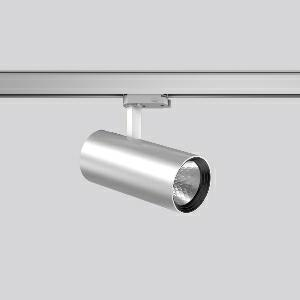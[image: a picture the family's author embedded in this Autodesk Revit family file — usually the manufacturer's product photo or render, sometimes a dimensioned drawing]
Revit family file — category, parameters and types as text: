
# Revit family: deecos_s_mini_742196_004_3_76_3f5c
name_source: partatom
category: Lighting Fixtures
units: mm (PartAtom-declared; Revit-internal decimal feet)

## family parameters
Cut with Voids When Loaded = No
Host = Face
Light Source = No
Part Type = Normal
Room Calculation Point = No
Round Connector Dimension = Use Diameter
Shared = No

## types (1)
- DEECOS S mini (1 x LED Modul 935, 2500 lm, 3500)
    Apparent Load = 20 VA
    Approval mark = CE
    CIE Flux Codes = 99 100 100 100 100
    Color Rendering = 92
    Color Temperature = 3500
    Default Elevation = 1800 mm
    Description = Series: DEECOS S mini
LED surface-mounted projector in modern design with no visible cooling ribs. Housing: die-cast aluminium, powder-coated. Rotation range: 356°. Swivel range: 90°. Black plastic ring and recessed LED to prevent glare from the side. Optical assembly with reflector made of MIRO-Silver with 98% total light reflection for outstanding efficiency - can be changed without tools. Best colour rendering index Ra>90. With adapter for RZB 3-circuit DALI tracks. Suitable for Track on ceiling, Wall track. High quality converter without flickering and stroboscopic effect. The following accessories can be mounted without use of tools: interchangeable lenses, decorative glasses, honeycomb louvre, clear and frosted diffusers, white interchangeable plastic ring. 
Colour: silver
Diameter: 87 mm
Height: 214 mm
Lamp: LED
Socket: without socket
Colour temperature: 3500K
Colour rendering index (CRI): 92
System power: 20 W
Rated luminous flux: 2500 lm
Luminous efficiency: 125 lm/W
Control gear: Converter, dimmable, DALI
Protection class: I
Type of protection: IP 20
    Height = 214 mm
    Lamp = 1 x LED Modul 935
    Lamp Light Flux = 2500 lm
    Lamp count = 1
    Length = 87 mm
    Lifetime = 50000 h
    Luminous efficacy = 125 lm/W
    Manufacturer = RZB
    ModVariant = No
    Model = 742196.004.3.76
    Mounting Place = Ceiling
    Mounting Type = Rail mounted
    Number of Poles = 1
    OnlyDefault = Yes
    Power Factor = 1
    Product Name = DEECOS S mini
    Product group = Track mounted projectors
    ProductGroupID = 301
    Protection Class = Protection class I
    Protection Degree = IP 20
    RLX_Detail_Level = 1
    RLX_Emergency_Light_Flux = 0 lm
    RLX_Emergency_Type = 0
    RLX_Emergency_Type_DB = No
    RlxData = <blob elided: 37349 chars, md5=465d9cad>
    Socket = socket
    Standby Power = 0 W
    System Light Flux = 2500 lm
    System Power = 20 W
    Type Comments = Product without accessories
    Type Image = 741926.004.jpg
    URL = http://relux.com
    VarID = ---
    Voltage = 230 V
    Voltage Range = 220-240 V
    Weight = 0.00 kg
    Width = 0 mm  [stored 0 ft]

note: [stored X ft] marks values corroborated as IEEE doubles in the binary element streams (Revit-internal decimal feet)

## geometry (parser evidence)
native form markers: Blend x4, Sweep x11
no freeform markers — native parametric forms only
